FCSTD DOCUMENT  (FreeCAD 0.21R33771 (Git))
Label: Assembly-SgancioViteCarro
License: All rights reserved
LicenseURL: http://en.wikipedia.org/wiki/All_rights_reserved
objects: App::DocumentObjectGroup×4, App::Link×4, PartDesign::CoordinateSystem×1, App::FeaturePython×1, App::Part×1, Part::FeaturePython×1, App::AnnotationLabel×1
note: 2 computed .brp shape members not serialized (recipe doc carries the construction recipe); baked Part::Feature solids carry a one-line shape summary decoded from their .brp
EXTERNAL_REF file=ChiocciolaMezzoSupporto.FCStd obj=LCS_HlafNut
EXTERNAL_REF file=FangiaHalfNut.FCStd obj=LCS_FlangiaHalfNut
EXTERNAL_REF file=ChiocciolaMezzoSupporto.FCStd obj=Body
EXTERNAL_REF file=FangiaHalfNut.FCStd obj=Body
EXTERNAL_REF file=CammaRotazioneHalfNut-160.FCStd obj=LCS_CammaHalfNut
EXTERNAL_REF file=CammaRotazioneHalfNut-160.FCStd obj=Body

FEATURE [App::DocumentObjectGroup] Parts
FEATURE [PartDesign::CoordinateSystem] LCS_Origin
  AttacherType = Attacher::AttachEngine3D
  MapMode = 2
  Support = -> [X_Axis]
FEATURE [App::DocumentObjectGroup] Constraints
FEATURE [App::FeaturePython] Variables  # WARN: FeaturePython — macro-defined, semantics opaque (R4)
  Type = App::PropertyContainer
FEATURE [App::DocumentObjectGroup] Configurations
FEATURE [App::Link] ChiocciolaMezzoSupporto_link  label="ChiocciolaMezzoSupporto-link"
  AttachedBy = #LCS_HlafNut
  AttachedTo = FlangiaHalfNut_link#LCS_FlangiaHalfNut
  AttachmentOffset = pos=(44,45,27) rot=(0,1,0;4.71239rad)
  LinkPlacement = pos=(44,45,27) rot=(0,1,0;4.71239rad)
  LinkedObject = -> <external ChiocciolaMezzoSupporto.FCStd>#Body
  Placement = pos=(44,45,27) rot=(0,1,0;4.71239rad)
  SolverId = Asm4EE
  expr: Placement = FlangiaHalfNut_link.Placement * FangiaHalfNut#LCS_FlangiaHalfNut.Placement * AttachmentOffset * ChiocciolaMezzoSupporto#LCS_HlafNut.Placement ^ -1
FEATURE [App::Link] ChiocciolaMezzoSupporto_2_link  label="ChiocciolaMezzoSupporto-2-link"
  AttachedBy = #LCS_HlafNut
  AttachedTo = ChiocciolaMezzoSupporto_link#LCS_HlafNut
  AttachmentOffset = pos=(0,0,28) rot=(1,0,0;3.14159rad)
  LinkPlacement = pos=(16,45,27) rot=(-0.707107,0,-0.707107;3.14159rad)
  LinkedObject = -> <external ChiocciolaMezzoSupporto.FCStd>#Body
  Placement = pos=(16,45,27) rot=(-0.707107,0,-0.707107;3.14159rad)
  SolverId = Asm4EE
  expr: Placement = ChiocciolaMezzoSupporto_link.Placement * ChiocciolaMezzoSupporto#LCS_HlafNut.Placement * AttachmentOffset * ChiocciolaMezzoSupporto#LCS_HlafNut.Placement ^ -1
FEATURE [App::Link] FlangiaHalfNut_link  label="FlangiaHalfNut-link"
  AttachedBy = #LCS_FlangiaHalfNut
  AttachedTo = Parent Assembly#LCS_Origin
  LinkedObject = -> <external FangiaHalfNut.FCStd>#Body
  SolverId = Asm4EE
  expr: Placement = LCS_Origin.Placement * AttachmentOffset * FangiaHalfNut#LCS_FlangiaHalfNut.Placement ^ -1
FEATURE [App::Link] CammaRotazioneHalfNut_160_link  label="CammaRotazioneHalfNut-160-link"
  AttachedBy = #LCS_CammaHalfNut
  AttachedTo = FlangiaHalfNut_link#LCS_FlangiaHalfNut
  AttachmentOffset = pos=(30,45,0) rot=(0,0,-1;4.71239rad)
  LinkPlacement = pos=(30,45,0) rot=(0,0,-1;4.71239rad)
  LinkedObject = -> <external CammaRotazioneHalfNut-160.FCStd>#Body
  Placement = pos=(30,45,0) rot=(0,0,-1;4.71239rad)
  SolverId = Asm4EE
  expr: Placement = FlangiaHalfNut_link.Placement * FangiaHalfNut#LCS_FlangiaHalfNut.Placement * AttachmentOffset * CammaRotazioneHalfNut_160#LCS_CammaHalfNut.Placement ^ -1
FEATURE [App::Part] Assembly
  AssemblyType = Part::Link
  Group = -> [LCS_Origin,Constraints,Variables,Configurations,ChiocciolaMezzoSupporto_link,ChiocciolaMezzoSupporto_2_link,FlangiaHalfNut_link,CammaRotazioneHalfNut_160_link]
  Origin = -> Origin
  Type = Assembly
FEATURE [Part::FeaturePython] DistPoints  # WARN: FeaturePython — macro-defined, semantics opaque (R4)
FEATURE [App::AnnotationLabel] MeasureLbl
  BasePosition = (0,45,0)
  LabelText = D = 90,00 mm
  TextPosition = (0,0,0)
FEATURE [App::DocumentObjectGroup] Measures
  Group = -> [DistPoints,MeasureLbl]

RESOLVED EXTERNAL PARTS (link-assembly join: the EXTERNAL_REF files above that resolve inside this repo's crawl, each included once):
---- part CammaRotazioneHalfNut-160.FCStd = doc fcstd_9a8f8aeae08e ----
FCSTD DOCUMENT  (FreeCAD 0.21R33771 (Git))
Label: CammaRotazioneHalfNut-160
License: All rights reserved
LicenseURL: http://en.wikipedia.org/wiki/All_rights_reserved
objects: Sketcher::SketchObject×6, App::MeasureDistance×5, Part::Spiral×2, PartDesign::Pocket×2, PartDesign::Pad×1, PartDesign::CoordinateSystem×1, PartDesign::Body×1
note: 16 computed .brp shape members not serialized (recipe doc carries the construction recipe); baked Part::Feature solids carry a one-line shape summary decoded from their .brp

FEATURE [Sketcher::SketchObject] Sketch
  FullyConstrained = true
  MapMode = 5
  Support = -> [XY_Plane]
  sketch-geometry (1):
    g0: Circle CenterX=0 CenterY=0 CenterZ=0 NormalX=0 NormalY=0 NormalZ=1 AngleXU=0 Radius=25
  constraints (2):
    c: Coincident(g0,g-1)
    c: Radius(g0) = 25
FEATURE [PartDesign::Pad] Pad
  Direction = (0,0,1)
  Length = 4
  Length2 = 10
  Profile = -> Sketch
  ReferenceAxis = -> Sketch [N_Axis]
  Type = 0
FEATURE [Part::Spiral] Spiral  label="Spirale"
  AttacherType = Attacher::AttachEngine3D
  Growth = 16
  Placement = pos=(0,0,0) rot=(0,0,1;3.14159rad)
  Radius = 15
  Rotations = 0.45
  SegmentLength = 1
FEATURE [Part::Spiral] Spiral001  label="Spirale001"
  AttacherType = Attacher::AttachEngine3D
  Growth = 16
  Placement = pos=(0,0,0) rot=(0,0,1;3.14159rad)
  Radius = 10
  Rotations = 0.45
  SegmentLength = 1
FEATURE [Sketcher::SketchObject] Sketch001
  FullyConstrained = false
  Placement = pos=(0,0,0) rot=(0,0,1;3.14159rad)
  sketch-geometry (1):
    g0: BSplineCurve PolesCount=9 KnotsCount=2 Degree=8 IsPeriodic=0
FEATURE [Sketcher::SketchObject] Sketch002
  FullyConstrained = false
  Placement = pos=(0,0,0) rot=(0,0,1;3.14159rad)
  sketch-geometry (1):
    g0: BSplineCurve PolesCount=9 KnotsCount=2 Degree=8 IsPeriodic=0
FEATURE [Sketcher::SketchObject] Sketch004
  FullyConstrained = false
  Placement = pos=(0,0,0) rot=(0,0,1;3.14159rad)
  sketch-geometry (2):
    g0: BSplineCurve PolesCount=9 KnotsCount=2 Degree=8 IsPeriodic=0
    g1: BSplineCurve PolesCount=9 KnotsCount=2 Degree=8 IsPeriodic=0
FEATURE [PartDesign::CoordinateSystem] LCS_CammaHalfNut
  AttacherType = Attacher::AttachEngine3D
FEATURE [Sketcher::SketchObject] Sketch008
  FullyConstrained = false
  Placement = pos=(0,0,0) rot=(0,0,1;3.14159rad)
  sketch-geometry (4):
    g0: BSplineCurve PolesCount=11 KnotsCount=2 Degree=10 IsPeriodic=0
    g1: BSplineCurve PolesCount=11 KnotsCount=2 Degree=10 IsPeriodic=0
    g2: ArcOfCircle CenterX=-18.7499 CenterY=6.0442 CenterZ=0 NormalX=0 NormalY=0 NormalZ=1 AngleXU=0 Radius=2.50042 StartAngle=2.80917 EndAngle=5.98729
    g3: ArcOfCircle CenterX=12.5 CenterY=-0.178417 CenterZ=0 NormalX=0 NormalY=0 NormalZ=1 AngleXU=0 Radius=2.50636 StartAngle=3.07035 EndAngle=6.35443
  constraints (4):
    c: Coincident(g2,g0)
    c: Coincident(g2,g1)
    c: Coincident(g3,g1)
    c: Coincident(g3,g0)
FEATURE [Sketcher::SketchObject] Sketch009
  FullyConstrained = false
  sketch-geometry (8):
    g0: BSplineCurve PolesCount=11 KnotsCount=2 Degree=10 IsPeriodic=0
    g1: BSplineCurve PolesCount=11 KnotsCount=2 Degree=10 IsPeriodic=0
    g2: ArcOfCircle CenterX=-18.7499 CenterY=6.0442 CenterZ=0 NormalX=0 NormalY=0 NormalZ=1 AngleXU=0 Radius=2.50042 StartAngle=2.80917 EndAngle=5.98729
    g3: ArcOfCircle CenterX=12.5 CenterY=-0.178417 CenterZ=0 NormalX=0 NormalY=0 NormalZ=1 AngleXU=0 Radius=2.50636 StartAngle=3.07035 EndAngle=6.35443
    g4: LineSegment StartX=-4 StartY=4 StartZ=0 EndX=4 EndY=4 EndZ=0
    g5: LineSegment StartX=4 StartY=4 StartZ=0 EndX=4 EndY=-4 EndZ=0
    g6: LineSegment StartX=4 StartY=-4 StartZ=0 EndX=-4 EndY=-4 EndZ=0
    g7: LineSegment StartX=-4 StartY=-4 StartZ=0 EndX=-4 EndY=4 EndZ=0
  constraints (16):
    c: Coincident(g2,g0)
    c: Coincident(g2,g1)
    c: Coincident(g3,g1)
    c: Coincident(g3,g0)
    c: Coincident(g4,g5)
    c: Coincident(g5,g6)
    c: Coincident(g6,g7)
    c: Coincident(g7,g4)
    c: Horizontal(g4)
    c: Horizontal(g6)
    c: Vertical(g5)
    c: Vertical(g7)
    c: DistanceY(g7,g7) = 8
    c: DistanceX(g4,g4) = 8
    c: DistanceX(g6,g-1) = 4
    c: DistanceY(g5,g-1) = 4
FEATURE [PartDesign::Pocket] Pocket
  BaseFeature = -> Pad
  Direction = (0,0,-1)
  Length = 5
  Length2 = 5
  Profile = -> Sketch008
  ReferenceAxis = -> Sketch008 [N_Axis]
  Reversed = true
  Type = 0
FEATURE [PartDesign::Pocket] Pocket001
  BaseFeature = -> Pocket
  Direction = (0,0,-1)
  Length = 5
  Length2 = 5
  Profile = -> Sketch009
  ReferenceAxis = -> Sketch009 [N_Axis]
  Reversed = true
  Type = 0
FEATURE [PartDesign::Body] Body
  Group = -> [Sketch,Pad,LCS_CammaHalfNut,Sketch008,Sketch009,Pocket,Pocket001]
  Origin = -> Origin
  Tip = -> Pocket001
FEATURE [App::MeasureDistance] Distance  label="Distance: 6,01 mm"
  Distance = 6.01178
  P1 = (-10.0081,0.175395,0)
  P2 = (-4,0.386232,0)
FEATURE [App::MeasureDistance] Distance001  label="Distance: 12,21 mm"
  Distance = 12.2089
  P1 = (16.1742,-4.93747,0)
  P2 = (3.97317,-5.37772,0)
FEATURE [App::MeasureDistance] Distance002  label="Distance: 14,28 mm"
  Distance = 14.2806
  P1 = (18.1238,0.345436,0)
  P2 = (3.84739,0,0)
FEATURE [App::MeasureDistance] Distance003  label="Distance: 9,85 mm"
  Distance = 9.84686
  P1 = (-0.729168,-13.8468,0)
  P2 = (-0.749632,-4,0)
FEATURE [App::MeasureDistance] Distance004  label="Distance: 9,99 mm"
  Distance = 9.98547
  P1 = (0.246943,-13.9839,0)
  P2 = (0.0679618,-4,0)
---- part ChiocciolaMezzoSupporto.FCStd = doc fcstd_22bf05dd260e ----
FCSTD DOCUMENT  (FreeCAD 0.21R33771 (Git))
Label: ChiocciolaMezzoSupporto
License: All rights reserved
LicenseURL: http://en.wikipedia.org/wiki/All_rights_reserved
objects: Sketcher::SketchObject×3, PartDesign::Pad×3, PartDesign::CoordinateSystem×1, PartDesign::Body×1
note: 11 computed .brp shape members not serialized (recipe doc carries the construction recipe); baked Part::Feature solids carry a one-line shape summary decoded from their .brp

FEATURE [Sketcher::SketchObject] Sketch
  FullyConstrained = true
  MapMode = 5
  Support = -> [XY_Plane]
  sketch-geometry (6):
    g0: LineSegment StartX=-20 StartY=15 StartZ=0 EndX=20 EndY=15 EndZ=0
    g1: LineSegment StartX=20 StartY=15 StartZ=0 EndX=20 EndY=0 EndZ=0
    g2: LineSegment StartX=20 StartY=0 StartZ=0 EndX=11 EndY=-2.17563e-05 EndZ=0
    g3: LineSegment StartX=-20 StartY=0 StartZ=0 EndX=-20 EndY=15 EndZ=0
    g4: ArcOfCircle CenterX=0 CenterY=0 CenterZ=0 NormalX=0 NormalY=0 NormalZ=1 AngleXU=0 Radius=11 StartAngle=6.28318 EndAngle=9.42478
    g5: LineSegment StartX=-11 StartY=0 StartZ=0 EndX=-20 EndY=0 EndZ=0
  constraints (17):
    c: Coincident(g0,g1)
    c: Coincident(g1,g2)
    c: Coincident(g5,g3)
    c: Coincident(g3,g0)
    c: Horizontal(g0)
    c: Vertical(g1)
    c: Vertical(g3)
    c: PointOnObject(g1,g-1)
    c: DistanceX(g0,g0) = 40
    c: DistanceY(g1,g1) = 15
    c: Symmetric(g5,g1,g-2)
    c: Coincident(g4,g-1)
    c: Radius(g4) = 11
    c: Coincident(g4,g5)
    c: Coincident(g4,g2)
    c: Equal(g5,g2)
    c: Horizontal(g5)
FEATURE [PartDesign::Pad] Pad
  Direction = (0,0,1)
  Length = 28
  Length2 = 10
  Profile = -> Sketch
  ReferenceAxis = -> Sketch [N_Axis]
  Type = 0
FEATURE [Sketcher::SketchObject] Sketch001
  FullyConstrained = true
  MapMode = 5
  Placement = pos=(-20,0,0) rot=(0.57735,-0.57735,-0.57735;2.0944rad)
  Support = -> [Pad]
  sketch-geometry (4):
    g0: LineSegment StartX=-30 StartY=32 StartZ=0 EndX=0 EndY=32 EndZ=0
    g1: LineSegment StartX=0 StartY=32 StartZ=0 EndX=0 EndY=-4 EndZ=0
    g2: LineSegment StartX=0 StartY=-4 StartZ=0 EndX=-30 EndY=-4 EndZ=0
    g3: LineSegment StartX=-30 StartY=-4 StartZ=0 EndX=-30 EndY=32 EndZ=0
  constraints (12):
    c: Coincident(g0,g1)
    c: Coincident(g1,g2)
    c: Coincident(g2,g3)
    c: Coincident(g3,g0)
    c: Horizontal(g0)
    c: Horizontal(g2)
    c: Vertical(g1)
    c: Vertical(g3)
    c: DistanceX(g0,g0) = 30
    c: PointOnObject(g-1,g1)
    c: DistanceY(g3,g3) = 36
    c: DistanceY(g1,g-1) = 4
FEATURE [PartDesign::Pad] Pad001
  BaseFeature = -> Pad
  Direction = (-1,0,0)
  Length = 3
  Length2 = 10
  Profile = -> Sketch001
  ReferenceAxis = -> Sketch001 [N_Axis]
  Type = 0
FEATURE [Sketcher::SketchObject] Sketch002
  FullyConstrained = false
  MapMode = 5
  Placement = pos=(-23,0,0) rot=(0.57735,-0.57735,-0.57735;2.0944rad)
  Support = -> [Pad001]
  sketch-geometry (2):
    g0: LineSegment StartX=-12.5 StartY=37.7883 StartZ=0 EndX=-12.5 EndY=-24.2198 EndZ=0
    g1: Circle CenterX=-12.5 CenterY=14 CenterZ=0 NormalX=0 NormalY=0 NormalZ=1 AngleXU=0 Radius=2.5
  constraints (5):
    c: Vertical(g0)
    c: PointOnObject(g1,g0)
    c: Radius(g1) = 2.5
    c: DistanceX(g0,g-1) = 12.5
    c: DistanceY(g-1,g1) = 14
FEATURE [PartDesign::Pad] Pad002
  BaseFeature = -> Pad001
  Direction = (-1,0,0)
  Length = 4
  Length2 = 10
  Profile = -> Sketch002
  ReferenceAxis = -> Sketch002 [N_Axis]
  Type = 0
FEATURE [PartDesign::CoordinateSystem] LCS_HlafNut
  AttacherType = Attacher::AttachEngine3D
FEATURE [PartDesign::Body] Body  label="Corpo"
  Group = -> [Sketch,Pad,Sketch001,Pad001,Sketch002,Pad002,LCS_HlafNut]
  Origin = -> Origin
  Tip = -> Pad002
---- part FangiaHalfNut.FCStd = doc fcstd_94a5a7e08d77 ----
FCSTD DOCUMENT  (FreeCAD 0.21R33771 (Git))
Label: FangiaHalfNut
License: All rights reserved
LicenseURL: http://en.wikipedia.org/wiki/All_rights_reserved
objects: Sketcher::SketchObject×4, PartDesign::Pocket×3, PartDesign::Pad×1, PartDesign::CoordinateSystem×1, PartDesign::Body×1
note: 14 computed .brp shape members not serialized (recipe doc carries the construction recipe); baked Part::Feature solids carry a one-line shape summary decoded from their .brp

FEATURE [Sketcher::SketchObject] Sketch
  FullyConstrained = true
  MapMode = 5
  Support = -> [XY_Plane]
  sketch-geometry (4):
    g0: LineSegment StartX=0 StartY=0 StartZ=0 EndX=60 EndY=0 EndZ=0
    g1: LineSegment StartX=60 StartY=0 StartZ=0 EndX=60 EndY=90 EndZ=0
    g2: LineSegment StartX=60 StartY=90 StartZ=0 EndX=0 EndY=90 EndZ=0
    g3: LineSegment StartX=0 StartY=90 StartZ=0 EndX=0 EndY=0 EndZ=0
  constraints (11):
    c: Coincident(g0,g1)
    c: Coincident(g1,g2)
    c: Coincident(g2,g3)
    c: Coincident(g3,g0)
    c: Horizontal(g0)
    c: Horizontal(g2)
    c: Vertical(g1)
    c: Vertical(g3)
    c: Coincident(g0,g-1)
    c: DistanceX(g0,g0) = 60
    c: DistanceY(g3,g3) = 90
FEATURE [PartDesign::Pad] Pad
  Direction = (0,0,1)
  Length = 10
  Length2 = 10
  Profile = -> Sketch
  ReferenceAxis = -> Sketch [N_Axis]
  Type = 0
FEATURE [Sketcher::SketchObject] Sketch001
  FullyConstrained = true
  MapMode = 5
  Placement = pos=(0,0,0) rot=(1,0,0;3.14159rad)
  Support = -> [Pad]
  sketch-geometry (4):
    g0: LineSegment StartX=15 StartY=-15 StartZ=0 EndX=45 EndY=-15 EndZ=0
    g1: LineSegment StartX=45 StartY=-15 StartZ=0 EndX=45 EndY=-75 EndZ=0
    g2: LineSegment StartX=45 StartY=-75 StartZ=0 EndX=15 EndY=-75 EndZ=0
    g3: LineSegment StartX=15 StartY=-75 StartZ=0 EndX=15 EndY=-15 EndZ=0
  constraints (12):
    c: Coincident(g0,g1)
    c: Coincident(g1,g2)
    c: Coincident(g2,g3)
    c: Coincident(g3,g0)
    c: Horizontal(g0)
    c: Horizontal(g2)
    c: Vertical(g1)
    c: Vertical(g3)
    c: DistanceY(g3,g3) = 60
    c: DistanceX(g0,g0) = 30
    c: DistanceX(g-1,g0) = 15
    c: DistanceY(g0,g-1) = 15
FEATURE [PartDesign::Pocket] Pocket
  BaseFeature = -> Pad
  Direction = (0,0,1)
  Length = 5
  Length2 = 5
  Profile = -> Sketch001
  ReferenceAxis = -> Sketch001 [N_Axis]
  Type = 1
FEATURE [Sketcher::SketchObject] Sketch002
  FullyConstrained = true
  MapMode = 5
  Support = -> [XY_Plane]
  sketch-geometry (4):
    g0: LineSegment StartX=48 StartY=80 StartZ=0 EndX=12 EndY=80 EndZ=0
    g1: LineSegment StartX=12 StartY=80 StartZ=0 EndX=12 EndY=10 EndZ=0
    g2: LineSegment StartX=12 StartY=10 StartZ=0 EndX=48 EndY=10 EndZ=0
    g3: LineSegment StartX=48 StartY=10 StartZ=0 EndX=48 EndY=80 EndZ=0
  constraints (12):
    c: Coincident(g0,g1)
    c: Coincident(g1,g2)
    c: Coincident(g2,g3)
    c: Coincident(g3,g0)
    c: Horizontal(g0)
    c: Horizontal(g2)
    c: Vertical(g1)
    c: Vertical(g3)
    c: DistanceX(g0,g0) = 36
    c: DistanceY(g3,g3) = 70
    c: DistanceX(g-1,g1) = 12
    c: DistanceY(g-1,g1) = 10
FEATURE [PartDesign::Pocket] Pocket001
  BaseFeature = -> Pocket
  Direction = (0,0,-1)
  Length = 7.5
  Length2 = 5
  Profile = -> Sketch002
  ReferenceAxis = -> Sketch002 [N_Axis]
  Reversed = true
  Type = 0
FEATURE [Sketcher::SketchObject] Sketch003
  FullyConstrained = true
  MapMode = 5
  Support = -> [XY_Plane]
  sketch-geometry (1):
    g0: Circle CenterX=30 CenterY=45 CenterZ=0 NormalX=0 NormalY=0 NormalZ=1 AngleXU=0 Radius=25.5
  constraints (3):
    c: Radius(g0) = 25.5
    c: DistanceY(g-1,g0) = 45
    c: DistanceX(g-1,g0) = 30
FEATURE [PartDesign::Pocket] Pocket002
  BaseFeature = -> Pocket001
  Direction = (0,0,-1)
  Length = 5
  Length2 = 5
  Profile = -> Sketch003
  ReferenceAxis = -> Sketch003 [N_Axis]
  Reversed = true
  Type = 0
FEATURE [PartDesign::CoordinateSystem] LCS_FlangiaHalfNut
  AttacherType = Attacher::AttachEngine3D
FEATURE [PartDesign::Body] Body  label="Corpo"
  Group = -> [Sketch,Pad,Sketch001,Pocket,Sketch002,Pocket001,Sketch003,Pocket002,LCS_FlangiaHalfNut]
  Origin = -> Origin
  Tip = -> Pocket002
